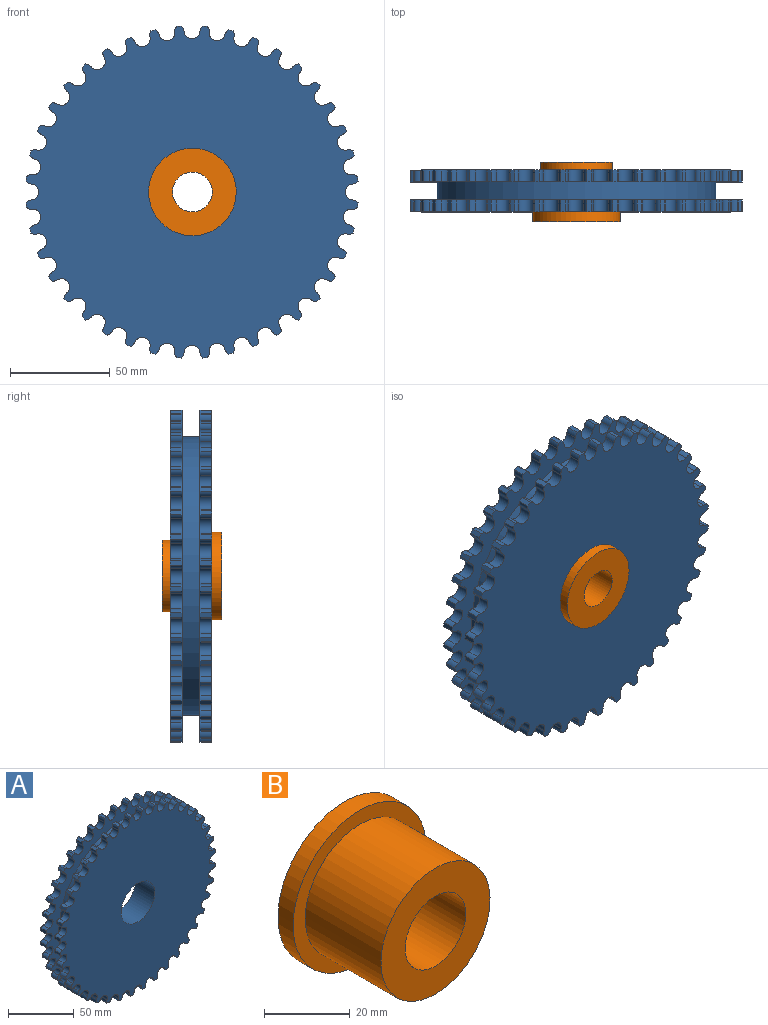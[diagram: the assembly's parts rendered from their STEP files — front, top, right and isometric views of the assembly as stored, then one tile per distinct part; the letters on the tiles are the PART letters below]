
ASSEMBLY  parts=2 mates=1
PART A: 326 faces, bbox 166.7x21x166.7 mm
  f0: cylinder r=4mm len=6mm, axis (0,-1,0), area 18.7mm2, adj f1,f159,f160,f161
  f1: cylinder r=4mm len=7.89mm, axis (0,-1,0), area 71.6mm2, adj f0,f2,f160,f161
  f2: cylinder r=4mm len=6mm, axis (0,-1,0), area 18.7mm2, adj f1,f3,f160,f161
  f3: cylinder r=83.71mm len=6mm, axis (0,-1,0), area 14.3mm2, adj f2,f4,f160,f161
  f4: cylinder r=4mm len=6mm, axis (0,-1,0), area 18.7mm2, adj f3,f5,f160,f161
  f5: cylinder r=4mm len=7.98mm, axis (0,-1,0), area 71.6mm2, adj f4,f6,f160,f161
  f6: cylinder r=4mm len=6mm, axis (0,-1,0), area 18.7mm2, adj f5,f7,f160,f161
  f7: cylinder r=83.71mm len=6mm, axis (0,-1,0), area 14.3mm2, adj f6,f8,f160,f161
  f8: cylinder r=4mm len=6mm, axis (0,-1,0), area 18.7mm2, adj f7,f9,f160,f161
  f9: cylinder r=4mm len=7.89mm, axis (0,-1,0), area 71.6mm2, adj f8,f10,f160,f161
  f10: cylinder r=4mm len=6mm, axis (0,-1,0), area 18.7mm2, adj f9,f11,f160,f161
  f11: cylinder r=83.71mm len=6mm, axis (0,-1,0), area 14.3mm2, adj f10,f12,f160,f161
  f12: cylinder r=4mm len=6mm, axis (0,-1,0), area 18.7mm2, adj f11,f13,f160,f161
  f13: cylinder r=4mm len=7.7mm, axis (0,-1,0), area 71.6mm2, adj f12,f14,f160,f161
  f14: cylinder r=4mm len=6mm, axis (0,-1,0), area 18.7mm2, adj f13,f15,f160,f161
  f15: cylinder r=83.71mm len=6mm, axis (0,-1,0), area 14.3mm2, adj f14,f16,f160,f161
  f16: cylinder r=4mm len=6mm, axis (0,-1,0), area 18.7mm2, adj f15,f17,f160,f161
  f17: cylinder r=4mm len=7.41mm, axis (0,-1,0), area 71.6mm2, adj f16,f18,f160,f161
  f18: cylinder r=4mm len=6mm, axis (0,-1,0), area 18.7mm2, adj f17,f19,f160,f161
  f19: cylinder r=83.71mm len=6mm, axis (0,-1,0), area 14.3mm2, adj f18,f20,f160,f161
  f20: cylinder r=4mm len=6mm, axis (0,-1,0), area 18.7mm2, adj f19,f21,f160,f161
  f21: cylinder r=4mm len=7.04mm, axis (0,-1,0), area 71.6mm2, adj f20,f22,f160,f161
  f22: cylinder r=4mm len=6mm, axis (0,-1,0), area 18.7mm2, adj f21,f23,f160,f161
  f23: cylinder r=83.71mm len=6mm, axis (0,-1,0), area 14.3mm2, adj f22,f24,f160,f161
  f24: cylinder r=4mm len=6mm, axis (0,-1,0), area 18.7mm2, adj f23,f25,f160,f161
  f25: cylinder r=4mm len=6.6mm, axis (0,-1,0), area 71.6mm2, adj f24,f26,f160,f161
  f26: cylinder r=4mm len=6mm, axis (0,-1,0), area 18.7mm2, adj f25,f27,f160,f161
  f27: cylinder r=83.71mm len=6mm, axis (0,-1,0), area 14.3mm2, adj f26,f28,f160,f161
  f28: cylinder r=4mm len=6mm, axis (0,-1,0), area 18.7mm2, adj f27,f29,f160,f161
  f29: cylinder r=4mm len=7.04mm, axis (0,-1,0), area 71.6mm2, adj f28,f30,f160,f161
  f30: cylinder r=4mm len=6mm, axis (0,-1,0), area 18.7mm2, adj f29,f31,f160,f161
  f31: cylinder r=83.71mm len=6mm, axis (0,-1,0), area 14.3mm2, adj f30,f32,f160,f161
  f32: cylinder r=4mm len=6mm, axis (0,-1,0), area 18.7mm2, adj f31,f33,f160,f161
  f33: cylinder r=4mm len=7.41mm, axis (0,-1,0), area 71.6mm2, adj f32,f34,f160,f161
  f34: cylinder r=4mm len=6mm, axis (0,-1,0), area 18.7mm2, adj f33,f35,f160,f161
  f35: cylinder r=83.71mm len=6mm, axis (0,-1,0), area 14.3mm2, adj f34,f36,f160,f161
  f36: cylinder r=4mm len=6mm, axis (0,-1,0), area 18.7mm2, adj f35,f37,f160,f161
  f37: cylinder r=4mm len=7.7mm, axis (0,-1,0), area 71.6mm2, adj f36,f38,f160,f161
  f38: cylinder r=4mm len=6mm, axis (0,-1,0), area 18.7mm2, adj f37,f39,f160,f161
  f39: cylinder r=83.71mm len=6mm, axis (0,-1,0), area 14.3mm2, adj f38,f40,f160,f161
  f40: cylinder r=4mm len=6mm, axis (0,-1,0), area 18.7mm2, adj f39,f41,f160,f161
  f41: cylinder r=4mm len=7.89mm, axis (0,-1,0), area 71.6mm2, adj f40,f42,f160,f161
  f42: cylinder r=4mm len=6mm, axis (0,-1,0), area 18.7mm2, adj f41,f43,f160,f161
  f43: cylinder r=83.71mm len=6mm, axis (0,-1,0), area 14.3mm2, adj f42,f44,f160,f161
  f44: cylinder r=4mm len=6mm, axis (0,-1,0), area 18.7mm2, adj f43,f45,f160,f161
  f45: cylinder r=4mm len=7.98mm, axis (0,-1,0), area 71.6mm2, adj f44,f46,f160,f161
  f46: cylinder r=4mm len=6mm, axis (0,-1,0), area 18.7mm2, adj f45,f47,f160,f161
  f47: cylinder r=83.71mm len=6mm, axis (0,-1,0), area 14.3mm2, adj f46,f48,f160,f161
  f48: cylinder r=4mm len=6mm, axis (0,-1,0), area 18.7mm2, adj f47,f49,f160,f161
  f49: cylinder r=4mm len=7.89mm, axis (0,-1,0), area 71.6mm2, adj f48,f50,f160,f161
  f50: cylinder r=4mm len=6mm, axis (0,-1,0), area 18.7mm2, adj f49,f51,f160,f161
  f51: cylinder r=83.71mm len=6mm, axis (0,-1,0), area 14.3mm2, adj f50,f52,f160,f161
  f52: cylinder r=4mm len=6mm, axis (0,-1,0), area 18.7mm2, adj f51,f53,f160,f161
  f53: cylinder r=4mm len=7.7mm, axis (0,-1,0), area 71.6mm2, adj f52,f54,f160,f161
  f54: cylinder r=4mm len=6mm, axis (0,-1,0), area 18.7mm2, adj f53,f55,f160,f161
  f55: cylinder r=83.71mm len=6mm, axis (0,-1,0), area 14.3mm2, adj f54,f56,f160,f161
  f56: cylinder r=4mm len=6mm, axis (0,-1,0), area 18.7mm2, adj f55,f57,f160,f161
  f57: cylinder r=4mm len=7.41mm, axis (0,-1,0), area 71.6mm2, adj f56,f58,f160,f161
  f58: cylinder r=4mm len=6mm, axis (0,-1,0), area 18.7mm2, adj f57,f59,f160,f161
  f59: cylinder r=83.71mm len=6mm, axis (0,-1,0), area 14.3mm2, adj f58,f60,f160,f161
  f60: cylinder r=4mm len=6mm, axis (0,-1,0), area 18.7mm2, adj f59,f61,f160,f161
  f61: cylinder r=4mm len=7.04mm, axis (0,-1,0), area 71.6mm2, adj f60,f62,f160,f161
  f62: cylinder r=4mm len=6mm, axis (0,-1,0), area 18.7mm2, adj f61,f63,f160,f161
  f63: cylinder r=83.71mm len=6mm, axis (0,-1,0), area 14.3mm2, adj f62,f64,f160,f161
  f64: cylinder r=4mm len=6mm, axis (0,-1,0), area 18.7mm2, adj f63,f65,f160,f161
  f65: cylinder r=4mm len=6.6mm, axis (0,-1,0), area 71.6mm2, adj f64,f66,f160,f161
  f66: cylinder r=4mm len=6mm, axis (0,-1,0), area 18.7mm2, adj f65,f67,f160,f161
  f67: cylinder r=83.71mm len=6mm, axis (0,-1,0), area 14.3mm2, adj f66,f68,f160,f161
  f68: cylinder r=4mm len=6mm, axis (0,-1,0), area 18.7mm2, adj f67,f69,f160,f161
  f69: cylinder r=4mm len=7.04mm, axis (0,-1,0), area 71.6mm2, adj f68,f70,f160,f161
  f70: cylinder r=4mm len=6mm, axis (0,-1,0), area 18.7mm2, adj f69,f71,f160,f161
  f71: cylinder r=83.71mm len=6mm, axis (0,-1,0), area 14.3mm2, adj f70,f72,f160,f161
  f72: cylinder r=4mm len=6mm, axis (0,-1,0), area 18.7mm2, adj f71,f73,f160,f161
  f73: cylinder r=4mm len=7.41mm, axis (0,-1,0), area 71.6mm2, adj f72,f74,f160,f161
  f74: cylinder r=4mm len=6mm, axis (0,-1,0), area 18.7mm2, adj f73,f75,f160,f161
  f75: cylinder r=83.71mm len=6mm, axis (0,-1,0), area 14.3mm2, adj f74,f76,f160,f161
  f76: cylinder r=4mm len=6mm, axis (0,-1,0), area 18.7mm2, adj f75,f77,f160,f161
  f77: cylinder r=4mm len=7.7mm, axis (0,-1,0), area 71.6mm2, adj f76,f78,f160,f161
  f78: cylinder r=4mm len=6mm, axis (0,-1,0), area 18.7mm2, adj f77,f79,f160,f161
  f79: cylinder r=83.71mm len=6mm, axis (0,-1,0), area 14.3mm2, adj f78,f80,f160,f161
  f80: cylinder r=4mm len=6mm, axis (0,-1,0), area 18.7mm2, adj f79,f81,f160,f161
  f81: cylinder r=4mm len=7.89mm, axis (0,-1,0), area 71.6mm2, adj f80,f82,f160,f161
  f82: cylinder r=4mm len=6mm, axis (0,-1,0), area 18.7mm2, adj f81,f83,f160,f161
  f83: cylinder r=83.71mm len=6mm, axis (0,-1,0), area 14.3mm2, adj f82,f84,f160,f161
  f84: cylinder r=4mm len=6mm, axis (0,-1,0), area 18.7mm2, adj f83,f85,f160,f161
  f85: cylinder r=4mm len=7.98mm, axis (0,-1,0), area 71.6mm2, adj f84,f86,f160,f161
  f86: cylinder r=4mm len=6mm, axis (0,-1,0), area 18.7mm2, adj f85,f87,f160,f161
  f87: cylinder r=83.71mm len=6mm, axis (0,-1,0), area 14.3mm2, adj f86,f88,f160,f161
  f88: cylinder r=4mm len=6mm, axis (0,-1,0), area 18.7mm2, adj f87,f89,f160,f161
  f89: cylinder r=4mm len=7.89mm, axis (0,-1,0), area 71.6mm2, adj f88,f90,f160,f161
  f90: cylinder r=4mm len=6mm, axis (0,-1,0), area 18.7mm2, adj f89,f91,f160,f161
  f91: cylinder r=83.71mm len=6mm, axis (0,-1,0), area 14.3mm2, adj f90,f92,f160,f161
  f92: cylinder r=4mm len=6mm, axis (0,-1,0), area 18.7mm2, adj f91,f93,f160,f161
  f93: cylinder r=4mm len=7.7mm, axis (0,-1,0), area 71.6mm2, adj f92,f94,f160,f161
  f94: cylinder r=4mm len=6mm, axis (0,-1,0), area 18.7mm2, adj f93,f95,f160,f161
  f95: cylinder r=83.71mm len=6mm, axis (0,-1,0), area 14.3mm2, adj f94,f96,f160,f161
  f96: cylinder r=4mm len=6mm, axis (0,-1,0), area 18.7mm2, adj f95,f97,f160,f161
  f97: cylinder r=4mm len=7.41mm, axis (0,-1,0), area 71.6mm2, adj f96,f98,f160,f161
  f98: cylinder r=4mm len=6mm, axis (0,-1,0), area 18.7mm2, adj f97,f99,f160,f161
  f99: cylinder r=83.71mm len=6mm, axis (0,-1,0), area 14.3mm2, adj f98,f100,f160,f161
  f100: cylinder r=4mm len=6mm, axis (0,-1,0), area 18.7mm2, adj f99,f101,f160,f161
  f101: cylinder r=4mm len=7.04mm, axis (0,-1,0), area 71.6mm2, adj f100,f102,f160,f161
  f102: cylinder r=4mm len=6mm, axis (0,-1,0), area 18.7mm2, adj f101,f103,f160,f161
  f103: cylinder r=83.71mm len=6mm, axis (0,-1,0), area 14.3mm2, adj f102,f104,f160,f161
  f104: cylinder r=4mm len=6mm, axis (0,-1,0), area 18.7mm2, adj f103,f105,f160,f161
  f105: cylinder r=4mm len=6.6mm, axis (0,-1,0), area 71.6mm2, adj f104,f106,f160,f161
  f106: cylinder r=4mm len=6mm, axis (0,-1,0), area 18.7mm2, adj f105,f107,f160,f161
  f107: cylinder r=83.71mm len=6mm, axis (0,-1,0), area 14.3mm2, adj f106,f108,f160,f161
  f108: cylinder r=4mm len=6mm, axis (0,-1,0), area 18.7mm2, adj f107,f109,f160,f161
  f109: cylinder r=4mm len=7.04mm, axis (0,-1,0), area 71.6mm2, adj f108,f110,f160,f161
  f110: cylinder r=4mm len=6mm, axis (0,-1,0), area 18.7mm2, adj f109,f111,f160,f161
  f111: cylinder r=83.71mm len=6mm, axis (0,-1,0), area 14.3mm2, adj f110,f112,f160,f161
  f112: cylinder r=4mm len=6mm, axis (0,-1,0), area 18.7mm2, adj f111,f113,f160,f161
  f113: cylinder r=4mm len=7.41mm, axis (0,-1,0), area 71.6mm2, adj f112,f114,f160,f161
  f114: cylinder r=4mm len=6mm, axis (0,-1,0), area 18.7mm2, adj f113,f115,f160,f161
  f115: cylinder r=83.71mm len=6mm, axis (0,-1,0), area 14.3mm2, adj f114,f116,f160,f161
  f116: cylinder r=4mm len=6mm, axis (0,-1,0), area 18.7mm2, adj f115,f117,f160,f161
  f117: cylinder r=4mm len=7.7mm, axis (0,-1,0), area 71.6mm2, adj f116,f118,f160,f161
  f118: cylinder r=4mm len=6mm, axis (0,-1,0), area 18.7mm2, adj f117,f119,f160,f161
  f119: cylinder r=83.71mm len=6mm, axis (0,-1,0), area 14.3mm2, adj f118,f120,f160,f161
  f120: cylinder r=4mm len=6mm, axis (0,-1,0), area 18.7mm2, adj f119,f121,f160,f161
  f121: cylinder r=4mm len=7.89mm, axis (0,-1,0), area 71.6mm2, adj f120,f122,f160,f161
  f122: cylinder r=4mm len=6mm, axis (0,-1,0), area 18.7mm2, adj f121,f123,f160,f161
  f123: cylinder r=83.71mm len=6mm, axis (0,-1,0), area 14.3mm2, adj f122,f124,f160,f161
  f124: cylinder r=4mm len=6mm, axis (0,-1,0), area 18.7mm2, adj f123,f125,f160,f161
  f125: cylinder r=4mm len=7.98mm, axis (0,-1,0), area 71.6mm2, adj f124,f126,f160,f161
  f126: cylinder r=4mm len=6mm, axis (0,-1,0), area 18.7mm2, adj f125,f127,f160,f161
  f127: cylinder r=83.71mm len=6mm, axis (0,-1,0), area 14.3mm2, adj f126,f128,f160,f161
  f128: cylinder r=4mm len=6mm, axis (0,-1,0), area 18.7mm2, adj f127,f129,f160,f161
  f129: cylinder r=4mm len=7.89mm, axis (0,-1,0), area 71.6mm2, adj f128,f130,f160,f161
  f130: cylinder r=4mm len=6mm, axis (0,-1,0), area 18.7mm2, adj f129,f131,f160,f161
  f131: cylinder r=83.71mm len=6mm, axis (0,-1,0), area 14.3mm2, adj f130,f132,f160,f161
  f132: cylinder r=4mm len=6mm, axis (0,-1,0), area 18.7mm2, adj f131,f133,f160,f161
  f133: cylinder r=4mm len=7.7mm, axis (0,-1,0), area 71.6mm2, adj f132,f134,f160,f161
  f134: cylinder r=4mm len=6mm, axis (0,-1,0), area 18.7mm2, adj f133,f135,f160,f161
  f135: cylinder r=83.71mm len=6mm, axis (0,-1,0), area 14.3mm2, adj f134,f136,f160,f161
  f136: cylinder r=4mm len=6mm, axis (0,-1,0), area 18.7mm2, adj f135,f137,f160,f161
  f137: cylinder r=4mm len=7.41mm, axis (0,-1,0), area 71.6mm2, adj f136,f138,f160,f161
  f138: cylinder r=4mm len=6mm, axis (0,-1,0), area 18.7mm2, adj f137,f139,f160,f161
  f139: cylinder r=83.71mm len=6mm, axis (0,-1,0), area 14.3mm2, adj f138,f140,f160,f161
  f140: cylinder r=4mm len=6mm, axis (0,-1,0), area 18.7mm2, adj f139,f141,f160,f161
  f141: cylinder r=4mm len=7.04mm, axis (0,-1,0), area 71.6mm2, adj f140,f142,f160,f161
  f142: cylinder r=4mm len=6mm, axis (0,-1,0), area 18.7mm2, adj f141,f143,f160,f161
  f143: cylinder r=83.71mm len=6mm, axis (0,-1,0), area 14.3mm2, adj f142,f144,f160,f161
  f144: cylinder r=4mm len=6mm, axis (0,-1,0), area 18.7mm2, adj f143,f145,f160,f161
  f145: cylinder r=4mm len=6.6mm, axis (0,-1,0), area 71.6mm2, adj f144,f146,f160,f161
  f146: cylinder r=4mm len=6mm, axis (0,-1,0), area 18.7mm2, adj f145,f147,f160,f161
  f147: cylinder r=83.71mm len=6mm, axis (0,-1,0), area 14.3mm2, adj f146,f148,f160,f161
  f148: cylinder r=4mm len=6mm, axis (0,-1,0), area 18.7mm2, adj f147,f149,f160,f161
  f149: cylinder r=4mm len=7.04mm, axis (0,-1,0), area 71.6mm2, adj f148,f150,f160,f161
  f150: cylinder r=4mm len=6mm, axis (0,-1,0), area 18.7mm2, adj f149,f151,f160,f161
  f151: cylinder r=83.71mm len=6mm, axis (0,-1,0), area 14.3mm2, adj f150,f152,f160,f161
  f152: cylinder r=4mm len=6mm, axis (0,-1,0), area 18.7mm2, adj f151,f153,f160,f161
  f153: cylinder r=4mm len=7.41mm, axis (0,-1,0), area 71.6mm2, adj f152,f154,f160,f161
  f154: cylinder r=4mm len=6mm, axis (0,-1,0), area 18.7mm2, adj f153,f155,f160,f161
  f155: cylinder r=83.71mm len=6mm, axis (0,-1,0), area 14.3mm2, adj f154,f156,f160,f161
  f156: cylinder r=4mm len=6mm, axis (0,-1,0), area 18.7mm2, adj f155,f157,f160,f161
  f157: cylinder r=4mm len=7.7mm, axis (0,-1,0), area 71.6mm2, adj f156,f158,f160,f161
  f158: cylinder r=4mm len=6mm, axis (0,-1,0), area 18.7mm2, adj f157,f159,f160,f161
  f159: cylinder r=83.71mm len=6mm, axis (0,-1,0), area 14.3mm2, adj f0,f158,f160,f161
  f160: plane 166.67x166.67mm, normal (0,1,0), area 18969.4mm2, adj f0,f1,f2,f3,f4,f5,f6,f7
  f161: plane 166.67x166.67mm, normal (0,-1,0), area 4593.4mm2, adj f0,f1,f2,f3,f4,f5,f6,f7
  f162: cylinder r=4mm len=7.89mm, axis (0,-1,0), area 71.6mm2, adj f163,f321,f322,f323
  f163: cylinder r=4mm len=6mm, axis (0,-1,0), area 18.7mm2, adj f162,f164,f322,f323
  f164: cylinder r=83.71mm len=6mm, axis (0,-1,0), area 14.3mm2, adj f163,f165,f322,f323
  f165: cylinder r=4mm len=6mm, axis (0,-1,0), area 18.7mm2, adj f164,f166,f322,f323
  f166: cylinder r=4mm len=7.98mm, axis (0,-1,0), area 71.6mm2, adj f165,f167,f322,f323
  f167: cylinder r=4mm len=6mm, axis (0,-1,0), area 18.7mm2, adj f166,f168,f322,f323
  f168: cylinder r=83.71mm len=6mm, axis (0,-1,0), area 14.3mm2, adj f167,f169,f322,f323
  f169: cylinder r=4mm len=6mm, axis (0,-1,0), area 18.7mm2, adj f168,f170,f322,f323
  f170: cylinder r=4mm len=7.89mm, axis (0,-1,0), area 71.6mm2, adj f169,f171,f322,f323
  f171: cylinder r=4mm len=6mm, axis (0,-1,0), area 18.7mm2, adj f170,f172,f322,f323
  f172: cylinder r=83.71mm len=6mm, axis (0,-1,0), area 14.3mm2, adj f171,f173,f322,f323
  f173: cylinder r=4mm len=6mm, axis (0,-1,0), area 18.7mm2, adj f172,f174,f322,f323
  f174: cylinder r=4mm len=7.7mm, axis (0,-1,0), area 71.6mm2, adj f173,f175,f322,f323
  f175: cylinder r=4mm len=6mm, axis (0,-1,0), area 18.7mm2, adj f174,f176,f322,f323
  f176: cylinder r=83.71mm len=6mm, axis (0,-1,0), area 14.3mm2, adj f175,f177,f322,f323
  f177: cylinder r=4mm len=6mm, axis (0,-1,0), area 18.7mm2, adj f176,f178,f322,f323
  f178: cylinder r=4mm len=7.41mm, axis (0,-1,0), area 71.6mm2, adj f177,f179,f322,f323
  f179: cylinder r=4mm len=6mm, axis (0,-1,0), area 18.7mm2, adj f178,f180,f322,f323
  f180: cylinder r=83.71mm len=6mm, axis (0,-1,0), area 14.3mm2, adj f179,f181,f322,f323
  f181: cylinder r=4mm len=6mm, axis (0,-1,0), area 18.7mm2, adj f180,f182,f322,f323
  f182: cylinder r=4mm len=7.04mm, axis (0,-1,0), area 71.6mm2, adj f181,f183,f322,f323
  f183: cylinder r=4mm len=6mm, axis (0,-1,0), area 18.7mm2, adj f182,f184,f322,f323
  f184: cylinder r=83.71mm len=6mm, axis (0,-1,0), area 14.3mm2, adj f183,f185,f322,f323
  f185: cylinder r=4mm len=6mm, axis (0,-1,0), area 18.7mm2, adj f184,f186,f322,f323
  f186: cylinder r=4mm len=6.6mm, axis (0,-1,0), area 71.6mm2, adj f185,f187,f322,f323
  f187: cylinder r=4mm len=6mm, axis (0,-1,0), area 18.7mm2, adj f186,f188,f322,f323
  f188: cylinder r=83.71mm len=6mm, axis (0,-1,0), area 14.3mm2, adj f187,f189,f322,f323
  f189: cylinder r=4mm len=6mm, axis (0,-1,0), area 18.7mm2, adj f188,f190,f322,f323
  f190: cylinder r=4mm len=7.04mm, axis (0,-1,0), area 71.6mm2, adj f189,f191,f322,f323
  f191: cylinder r=4mm len=6mm, axis (0,-1,0), area 18.7mm2, adj f190,f192,f322,f323
  f192: cylinder r=83.71mm len=6mm, axis (0,-1,0), area 14.3mm2, adj f191,f193,f322,f323
  f193: cylinder r=4mm len=6mm, axis (0,-1,0), area 18.7mm2, adj f192,f194,f322,f323
  f194: cylinder r=4mm len=7.41mm, axis (0,-1,0), area 71.6mm2, adj f193,f195,f322,f323
  f195: cylinder r=4mm len=6mm, axis (0,-1,0), area 18.7mm2, adj f194,f196,f322,f323
  f196: cylinder r=83.71mm len=6mm, axis (0,-1,0), area 14.3mm2, adj f195,f197,f322,f323
  f197: cylinder r=4mm len=6mm, axis (0,-1,0), area 18.7mm2, adj f196,f198,f322,f323
  f198: cylinder r=4mm len=7.7mm, axis (0,-1,0), area 71.6mm2, adj f197,f199,f322,f323
  f199: cylinder r=4mm len=6mm, axis (0,-1,0), area 18.7mm2, adj f198,f200,f322,f323
  f200: cylinder r=83.71mm len=6mm, axis (0,-1,0), area 14.3mm2, adj f199,f201,f322,f323
  f201: cylinder r=4mm len=6mm, axis (0,-1,0), area 18.7mm2, adj f200,f202,f322,f323
  f202: cylinder r=4mm len=7.89mm, axis (0,-1,0), area 71.6mm2, adj f201,f203,f322,f323
  f203: cylinder r=4mm len=6mm, axis (0,-1,0), area 18.7mm2, adj f202,f204,f322,f323
  f204: cylinder r=83.71mm len=6mm, axis (0,-1,0), area 14.3mm2, adj f203,f205,f322,f323
  f205: cylinder r=4mm len=6mm, axis (0,-1,0), area 18.7mm2, adj f204,f206,f322,f323
  f206: cylinder r=4mm len=7.98mm, axis (0,-1,0), area 71.6mm2, adj f205,f207,f322,f323
  f207: cylinder r=4mm len=6mm, axis (0,-1,0), area 18.7mm2, adj f206,f208,f322,f323
  f208: cylinder r=83.71mm len=6mm, axis (0,-1,0), area 14.3mm2, adj f207,f209,f322,f323
  f209: cylinder r=4mm len=6mm, axis (0,-1,0), area 18.7mm2, adj f208,f210,f322,f323
  f210: cylinder r=4mm len=7.89mm, axis (0,-1,0), area 71.6mm2, adj f209,f211,f322,f323
  f211: cylinder r=4mm len=6mm, axis (0,-1,0), area 18.7mm2, adj f210,f212,f322,f323
  f212: cylinder r=83.71mm len=6mm, axis (0,-1,0), area 14.3mm2, adj f211,f213,f322,f323
  f213: cylinder r=4mm len=6mm, axis (0,-1,0), area 18.7mm2, adj f212,f214,f322,f323
  f214: cylinder r=4mm len=7.7mm, axis (0,-1,0), area 71.6mm2, adj f213,f215,f322,f323
  f215: cylinder r=4mm len=6mm, axis (0,-1,0), area 18.7mm2, adj f214,f216,f322,f323
  f216: cylinder r=83.71mm len=6mm, axis (0,-1,0), area 14.3mm2, adj f215,f217,f322,f323
  f217: cylinder r=4mm len=6mm, axis (0,-1,0), area 18.7mm2, adj f216,f218,f322,f323
  f218: cylinder r=4mm len=7.41mm, axis (0,-1,0), area 71.6mm2, adj f217,f219,f322,f323
  f219: cylinder r=4mm len=6mm, axis (0,-1,0), area 18.7mm2, adj f218,f220,f322,f323
  f220: cylinder r=83.71mm len=6mm, axis (0,-1,0), area 14.3mm2, adj f219,f221,f322,f323
  f221: cylinder r=4mm len=6mm, axis (0,-1,0), area 18.7mm2, adj f220,f222,f322,f323
  f222: cylinder r=4mm len=7.04mm, axis (0,-1,0), area 71.6mm2, adj f221,f223,f322,f323
  f223: cylinder r=4mm len=6mm, axis (0,-1,0), area 18.7mm2, adj f222,f224,f322,f323
  f224: cylinder r=83.71mm len=6mm, axis (0,-1,0), area 14.3mm2, adj f223,f225,f322,f323
  f225: cylinder r=4mm len=6mm, axis (0,-1,0), area 18.7mm2, adj f224,f226,f322,f323
  f226: cylinder r=4mm len=6.6mm, axis (0,-1,0), area 71.6mm2, adj f225,f227,f322,f323
  f227: cylinder r=4mm len=6mm, axis (0,-1,0), area 18.7mm2, adj f226,f228,f322,f323
  f228: cylinder r=83.71mm len=6mm, axis (0,-1,0), area 14.3mm2, adj f227,f229,f322,f323
  f229: cylinder r=4mm len=6mm, axis (0,-1,0), area 18.7mm2, adj f228,f230,f322,f323
  f230: cylinder r=4mm len=7.04mm, axis (0,-1,0), area 71.6mm2, adj f229,f231,f322,f323
  f231: cylinder r=4mm len=6mm, axis (0,-1,0), area 18.7mm2, adj f230,f232,f322,f323
  f232: cylinder r=83.71mm len=6mm, axis (0,-1,0), area 14.3mm2, adj f231,f233,f322,f323
  f233: cylinder r=4mm len=6mm, axis (0,-1,0), area 18.7mm2, adj f232,f234,f322,f323
  f234: cylinder r=4mm len=7.41mm, axis (0,-1,0), area 71.6mm2, adj f233,f235,f322,f323
  f235: cylinder r=4mm len=6mm, axis (0,-1,0), area 18.7mm2, adj f234,f236,f322,f323
  f236: cylinder r=83.71mm len=6mm, axis (0,-1,0), area 14.3mm2, adj f235,f237,f322,f323
  f237: cylinder r=4mm len=6mm, axis (0,-1,0), area 18.7mm2, adj f236,f238,f322,f323
  f238: cylinder r=4mm len=7.7mm, axis (0,-1,0), area 71.6mm2, adj f237,f239,f322,f323
  f239: cylinder r=4mm len=6mm, axis (0,-1,0), area 18.7mm2, adj f238,f240,f322,f323
  f240: cylinder r=83.71mm len=6mm, axis (0,-1,0), area 14.3mm2, adj f239,f241,f322,f323
  f241: cylinder r=4mm len=6mm, axis (0,-1,0), area 18.7mm2, adj f240,f242,f322,f323
  f242: cylinder r=4mm len=7.89mm, axis (0,-1,0), area 71.6mm2, adj f241,f243,f322,f323
  f243: cylinder r=4mm len=6mm, axis (0,-1,0), area 18.7mm2, adj f242,f244,f322,f323
  f244: cylinder r=83.71mm len=6mm, axis (0,-1,0), area 14.3mm2, adj f243,f245,f322,f323
  f245: cylinder r=4mm len=6mm, axis (0,-1,0), area 18.7mm2, adj f244,f246,f322,f323
  f246: cylinder r=4mm len=7.98mm, axis (0,-1,0), area 71.6mm2, adj f245,f247,f322,f323
  f247: cylinder r=4mm len=6mm, axis (0,-1,0), area 18.7mm2, adj f246,f248,f322,f323
  f248: cylinder r=83.71mm len=6mm, axis (0,-1,0), area 14.3mm2, adj f247,f249,f322,f323
  f249: cylinder r=4mm len=6mm, axis (0,-1,0), area 18.7mm2, adj f248,f250,f322,f323
  f250: cylinder r=4mm len=7.89mm, axis (0,-1,0), area 71.6mm2, adj f249,f251,f322,f323
  f251: cylinder r=4mm len=6mm, axis (0,-1,0), area 18.7mm2, adj f250,f252,f322,f323
  f252: cylinder r=83.71mm len=6mm, axis (0,-1,0), area 14.3mm2, adj f251,f253,f322,f323
  f253: cylinder r=4mm len=6mm, axis (0,-1,0), area 18.7mm2, adj f252,f254,f322,f323
  f254: cylinder r=4mm len=7.7mm, axis (0,-1,0), area 71.6mm2, adj f253,f255,f322,f323
  f255: cylinder r=4mm len=6mm, axis (0,-1,0), area 18.7mm2, adj f254,f256,f322,f323
  f256: cylinder r=83.71mm len=6mm, axis (0,-1,0), area 14.3mm2, adj f255,f257,f322,f323
  f257: cylinder r=4mm len=6mm, axis (0,-1,0), area 18.7mm2, adj f256,f258,f322,f323
  f258: cylinder r=4mm len=7.41mm, axis (0,-1,0), area 71.6mm2, adj f257,f259,f322,f323
  f259: cylinder r=4mm len=6mm, axis (0,-1,0), area 18.7mm2, adj f258,f260,f322,f323
  f260: cylinder r=83.71mm len=6mm, axis (0,-1,0), area 14.3mm2, adj f259,f261,f322,f323
  f261: cylinder r=4mm len=6mm, axis (0,-1,0), area 18.7mm2, adj f260,f262,f322,f323
  f262: cylinder r=4mm len=7.04mm, axis (0,-1,0), area 71.6mm2, adj f261,f263,f322,f323
  f263: cylinder r=4mm len=6mm, axis (0,-1,0), area 18.7mm2, adj f262,f264,f322,f323
  f264: cylinder r=83.71mm len=6mm, axis (0,-1,0), area 14.3mm2, adj f263,f265,f322,f323
  f265: cylinder r=4mm len=6mm, axis (0,-1,0), area 18.7mm2, adj f264,f266,f322,f323
  f266: cylinder r=4mm len=6.6mm, axis (0,-1,0), area 71.6mm2, adj f265,f267,f322,f323
  f267: cylinder r=4mm len=6mm, axis (0,-1,0), area 18.7mm2, adj f266,f268,f322,f323
  f268: cylinder r=83.71mm len=6mm, axis (0,-1,0), area 14.3mm2, adj f267,f269,f322,f323
  f269: cylinder r=4mm len=6mm, axis (0,-1,0), area 18.7mm2, adj f268,f270,f322,f323
  f270: cylinder r=4mm len=7.04mm, axis (0,-1,0), area 71.6mm2, adj f269,f271,f322,f323
  f271: cylinder r=4mm len=6mm, axis (0,-1,0), area 18.7mm2, adj f270,f272,f322,f323
  f272: cylinder r=83.71mm len=6mm, axis (0,-1,0), area 14.3mm2, adj f271,f273,f322,f323
  f273: cylinder r=4mm len=6mm, axis (0,-1,0), area 18.7mm2, adj f272,f274,f322,f323
  f274: cylinder r=4mm len=7.41mm, axis (0,-1,0), area 71.6mm2, adj f273,f275,f322,f323
  f275: cylinder r=4mm len=6mm, axis (0,-1,0), area 18.7mm2, adj f274,f276,f322,f323
  f276: cylinder r=83.71mm len=6mm, axis (0,-1,0), area 14.3mm2, adj f275,f277,f322,f323
  f277: cylinder r=4mm len=6mm, axis (0,-1,0), area 18.7mm2, adj f276,f278,f322,f323
  f278: cylinder r=4mm len=7.7mm, axis (0,-1,0), area 71.6mm2, adj f277,f279,f322,f323
  f279: cylinder r=4mm len=6mm, axis (0,-1,0), area 18.7mm2, adj f278,f280,f322,f323
  f280: cylinder r=83.71mm len=6mm, axis (0,-1,0), area 14.3mm2, adj f279,f281,f322,f323
  f281: cylinder r=4mm len=6mm, axis (0,-1,0), area 18.7mm2, adj f280,f282,f322,f323
  f282: cylinder r=4mm len=7.89mm, axis (0,-1,0), area 71.6mm2, adj f281,f283,f322,f323
  f283: cylinder r=4mm len=6mm, axis (0,-1,0), area 18.7mm2, adj f282,f284,f322,f323
  f284: cylinder r=83.71mm len=6mm, axis (0,-1,0), area 14.3mm2, adj f283,f285,f322,f323
  f285: cylinder r=4mm len=6mm, axis (0,-1,0), area 18.7mm2, adj f284,f286,f322,f323
  f286: cylinder r=4mm len=7.98mm, axis (0,-1,0), area 71.6mm2, adj f285,f287,f322,f323
  f287: cylinder r=4mm len=6mm, axis (0,-1,0), area 18.7mm2, adj f286,f288,f322,f323
  f288: cylinder r=83.71mm len=6mm, axis (0,-1,0), area 14.3mm2, adj f287,f289,f322,f323
  f289: cylinder r=4mm len=6mm, axis (0,-1,0), area 18.7mm2, adj f288,f290,f322,f323
  f290: cylinder r=4mm len=7.89mm, axis (0,-1,0), area 71.6mm2, adj f289,f291,f322,f323
  f291: cylinder r=4mm len=6mm, axis (0,-1,0), area 18.7mm2, adj f290,f292,f322,f323
  f292: cylinder r=83.71mm len=6mm, axis (0,-1,0), area 14.3mm2, adj f291,f293,f322,f323
  f293: cylinder r=4mm len=6mm, axis (0,-1,0), area 18.7mm2, adj f292,f294,f322,f323
  f294: cylinder r=4mm len=7.7mm, axis (0,-1,0), area 71.6mm2, adj f293,f295,f322,f323
  f295: cylinder r=4mm len=6mm, axis (0,-1,0), area 18.7mm2, adj f294,f296,f322,f323
  f296: cylinder r=83.71mm len=6mm, axis (0,-1,0), area 14.3mm2, adj f295,f297,f322,f323
  f297: cylinder r=4mm len=6mm, axis (0,-1,0), area 18.7mm2, adj f296,f298,f322,f323
  f298: cylinder r=4mm len=7.41mm, axis (0,-1,0), area 71.6mm2, adj f297,f299,f322,f323
  f299: cylinder r=4mm len=6mm, axis (0,-1,0), area 18.7mm2, adj f298,f300,f322,f323
  f300: cylinder r=83.71mm len=6mm, axis (0,-1,0), area 14.3mm2, adj f299,f301,f322,f323
  f301: cylinder r=4mm len=6mm, axis (0,-1,0), area 18.7mm2, adj f300,f302,f322,f323
  f302: cylinder r=4mm len=7.04mm, axis (0,-1,0), area 71.6mm2, adj f301,f303,f322,f323
  f303: cylinder r=4mm len=6mm, axis (0,-1,0), area 18.7mm2, adj f302,f304,f322,f323
  f304: cylinder r=83.71mm len=6mm, axis (0,-1,0), area 14.3mm2, adj f303,f305,f322,f323
  f305: cylinder r=4mm len=6mm, axis (0,-1,0), area 18.7mm2, adj f304,f306,f322,f323
  f306: cylinder r=4mm len=6.6mm, axis (0,-1,0), area 71.6mm2, adj f305,f307,f322,f323
  f307: cylinder r=4mm len=6mm, axis (0,-1,0), area 18.7mm2, adj f306,f308,f322,f323
  f308: cylinder r=83.71mm len=6mm, axis (0,-1,0), area 14.3mm2, adj f307,f309,f322,f323
  f309: cylinder r=4mm len=6mm, axis (0,-1,0), area 18.7mm2, adj f308,f310,f322,f323
  f310: cylinder r=4mm len=7.04mm, axis (0,-1,0), area 71.6mm2, adj f309,f311,f322,f323
  f311: cylinder r=4mm len=6mm, axis (0,-1,0), area 18.7mm2, adj f310,f312,f322,f323
  f312: cylinder r=83.71mm len=6mm, axis (0,-1,0), area 14.3mm2, adj f311,f313,f322,f323
  f313: cylinder r=4mm len=6mm, axis (0,-1,0), area 18.7mm2, adj f312,f314,f322,f323
  f314: cylinder r=4mm len=7.41mm, axis (0,-1,0), area 71.6mm2, adj f313,f315,f322,f323
  f315: cylinder r=4mm len=6mm, axis (0,-1,0), area 18.7mm2, adj f314,f316,f322,f323
  f316: cylinder r=83.71mm len=6mm, axis (0,-1,0), area 14.3mm2, adj f315,f317,f322,f323
  f317: cylinder r=4mm len=6mm, axis (0,-1,0), area 18.7mm2, adj f316,f318,f322,f323
  f318: cylinder r=4mm len=7.7mm, axis (0,-1,0), area 71.6mm2, adj f317,f319,f322,f323
  f319: cylinder r=4mm len=6mm, axis (0,-1,0), area 18.7mm2, adj f318,f320,f322,f323
  f320: cylinder r=83.71mm len=6mm, axis (0,-1,0), area 14.3mm2, adj f319,f321,f322,f323
  f321: cylinder r=4mm len=6mm, axis (0,-1,0), area 18.7mm2, adj f162,f320,f322,f323
  f322: plane 166.67x166.67mm, normal (0,1,0), area 4593.4mm2, adj f162,f163,f164,f165,f166,f167,f168,f169
  f323: plane 166.67x166.67mm, normal (0,-1,0), area 18969.4mm2, adj f162,f163,f164,f165,f166,f167,f168,f169
  f324: cylinder r=70mm len=140mm, axis (0,-1,0), area 3958.4mm2, adj f161,f322
  f325: cylinder r=18mm len=36mm, axis (0,-1,0), area 2375mm2, adj f160,f323
PART B: 6 faces, bbox 44x30x44 mm
  f0: cylinder r=22mm len=44mm, axis (0,-1,0), area 691.2mm2, adj f3,f5
  f1: plane 36x36mm, normal (0,-1,0), area 703.7mm2, adj f2,f4
  f2: cylinder r=10mm len=30mm, axis (0,-1,0), area 1885mm2, adj f1,f3
  f3: plane 44x44mm, normal (0,1,0), area 1206.4mm2, adj f0,f2
  f4: cylinder r=18mm len=36mm, axis (0,-1,0), area 2827.4mm2, adj f1,f5
  f5: plane 44x44mm, normal (0,-1,0), area 502.7mm2, adj f0,f4
PLACE A t=(-30.74,-21.71,-0.69)mm
PLACE B rot(axis=(1,0,0),180deg) t=(-30.54,3.29,-0.68)mm
MATE fastened B.f4 <-> A.f325  axis (0,1,0) through (-30.54,-21.71,-0.68)mm
